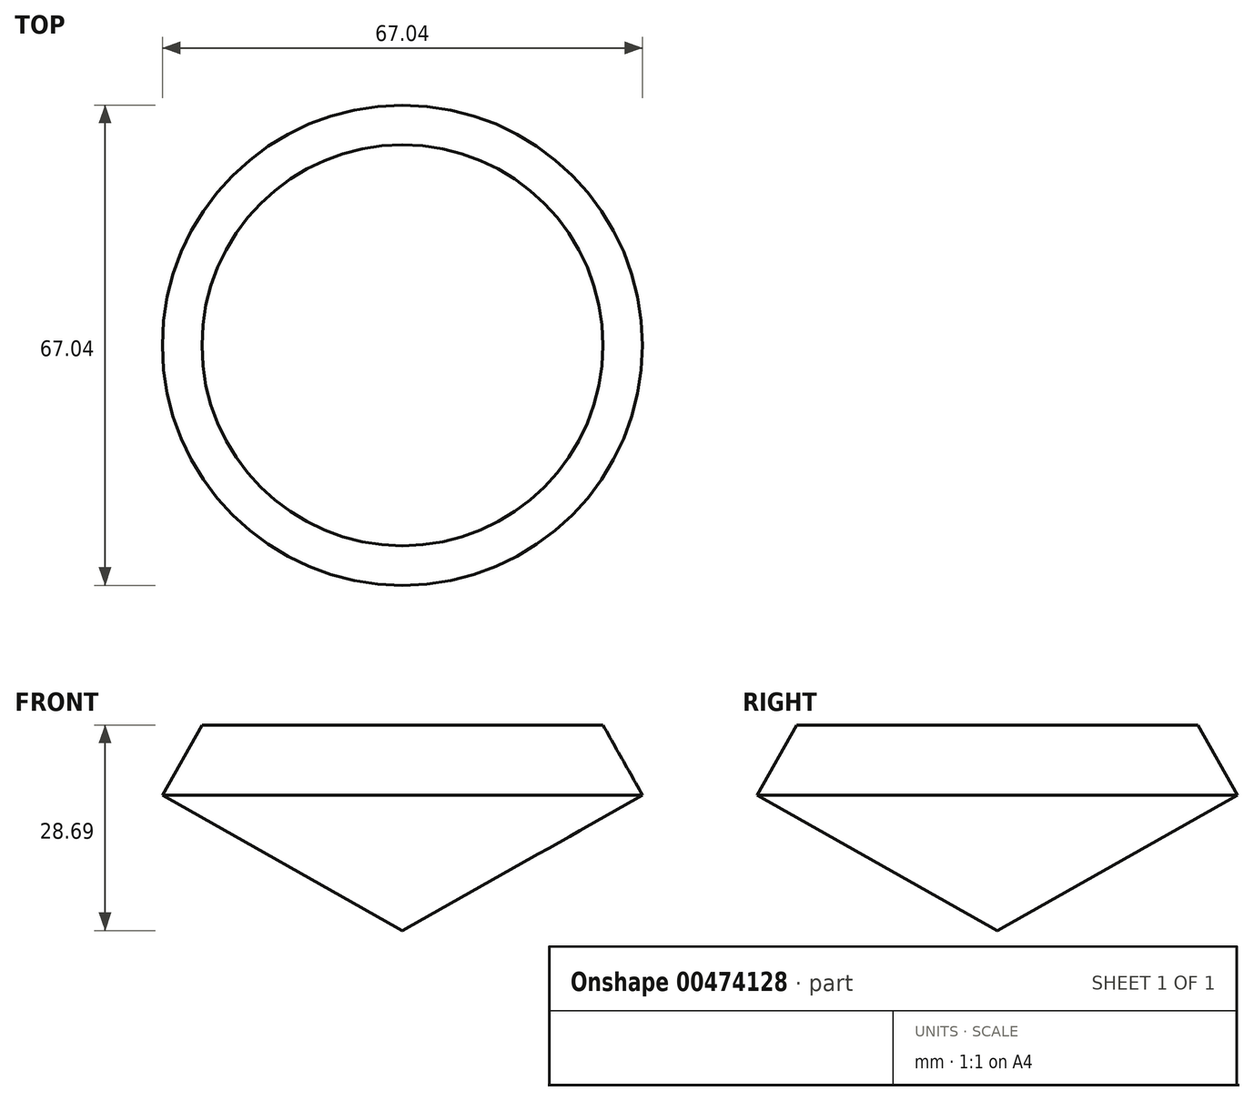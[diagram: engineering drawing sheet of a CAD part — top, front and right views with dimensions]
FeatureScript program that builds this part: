
annotation { "Feature Type Name" : "Feature", "Feature Type Description" : "" }
export const myFeature = defineFeature(function(context is Context, id is Id, definition is map)
    precondition{}
    {
        {
            var Q0;
            Q0=qCreatedBy(makeId("Front.planeOp"),FACE);
            var sketch = newSketch(context, id + "F0", { "sketchPlane" : qUnion([Q0])});
            skLineSegment(sketch, "E0", {"start": v(0, 0) * mm, "end": v(33.52, 18.9) * mm});
            skLineSegment(sketch, "E1", {"start": v(33.52, 18.9) * mm, "end": v(28, 28.69) * mm});
            skLineSegment(sketch, "E2", {"start": v(28, 28.69) * mm, "end": v(0, 28.69) * mm});
            skLineSegment(sketch, "E3", {"start": v(0, 28.69) * mm, "end": v(0, 0) * mm});
            skSolve(sketch);
        }
        {
            var Q0;
            Q0 = qSketchRegion(id + "F0", true);
            var Q1;
            Q1=sQuery(id+"F0.wireOp",EDGE,"E3");
            revolve(context, id + "F1", {"entities" : qUnion([Q0]), "axis" : qUnion([Q1]), "revolveType" : RevolveType.FULL});
        }
    });
